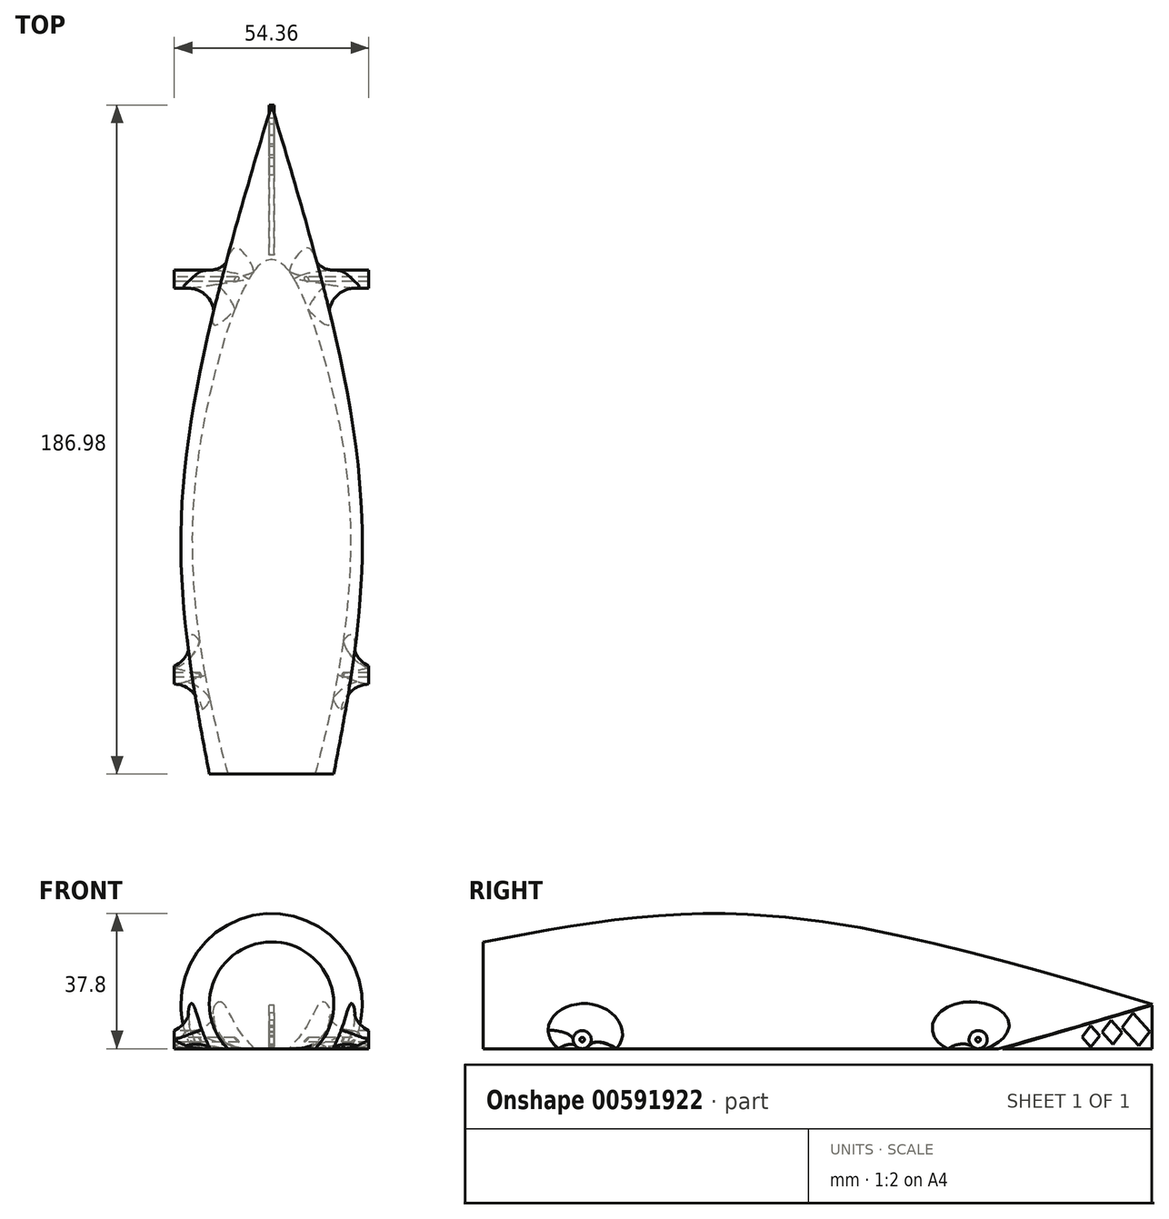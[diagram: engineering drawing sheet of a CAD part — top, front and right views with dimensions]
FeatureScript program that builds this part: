
annotation { "Feature Type Name" : "Feature", "Feature Type Description" : "" }
export const myFeature = defineFeature(function(context is Context, id is Id, definition is map)
    precondition{}
    {
        {
            var Q0;
            Q0=qCreatedBy(makeId("Top.planeOp"),FACE);
            cPlane(context, id + "F0", {"entities" : qUnion([Q0]), "cplaneType" : CPlaneType.OFFSET, "offset" : 7.37 * mm, "width" : 152.4 * mm, "height" : 152.4 * mm});
        }
        {
            var Q0;
            Q0=qCreatedBy(id+"F0.planeOp",FACE);
            var sketch = newSketch(context, id + "F1", { "sketchPlane" : qUnion([Q0])});
            skLineSegment(sketch, "E0", {"start": v(0, -99.9) * mm, "end": v(-17.4, -99.9) * mm});
            skFitSpline(sketch, "E1", {"points": [v(-17.4, -99.9) * mm, v(-24.98, -23.09) * mm, v(0, 87.08) * mm], "startDerivative": vector(-30.87, 162.6) * mm, "endDerivative": vector(62.7, 209.85) * mm});
            skLineSegment(sketch, "E2", {"start": v(0, -99.9) * mm, "end": v(0, 87.08) * mm});
            skSolve(sketch);
        }
        {
            var Q0;
            Q0=qSketchRegion(id+"F1",true);
            var Q1;
            Q1=sQuery(id+"F1.wireOp",EDGE,"E2");
            revolve(context, id + "F2", {"entities" : qUnion([Q0]), "axis" : qUnion([Q1]), "revolveType" : RevolveType.FULL});
        }
        {
            var Q0;
            Q0=qCreatedBy(makeId("Top.planeOp"),FACE);
            cPlane(context, id + "F3", {"entities" : qUnion([Q0]), "cplaneType" : CPlaneType.OFFSET, "offset" : 5.08 * mm, "oppositeDirection" : true, "width" : 152.4 * mm, "height" : 152.4 * mm});
        }
        {
            var Q0;
            Q0=qCreatedBy(id+"F3.planeOp",FACE);
            var sketch = newSketch(context, id + "F4", { "sketchPlane" : qUnion([Q0])});
            skLineSegment(sketch, "E3.bottom", {"start": v(73.32, 143.23) * mm, "end": v(-63.31, 143.23) * mm});
            skLineSegment(sketch, "E3.top", {"start": v(73.32, -152.23) * mm, "end": v(-63.31, -152.23) * mm});
            skLineSegment(sketch, "E3.left", {"start": v(73.32, 143.23) * mm, "end": v(73.32, -152.23) * mm});
            skLineSegment(sketch, "E3.right", {"start": v(-63.31, 143.23) * mm, "end": v(-63.31, -152.23) * mm});
            skSolve(sketch);
        }
        {
            var Q0;
            Q0=qSketchRegion(id+"F4",true);
            extrude(context, id + "F5", {"entities" : qUnion([Q0]), "operationType" : NewBodyOperationType.REMOVE, "oppositeDirection" : true, "depth" : 25.4 * mm, "offsetDistance" : 25.4 * mm});
        }
        {
            var Q0;
            Q0=qCreatedBy(makeId("Right.planeOp"),FACE);
            var sketch = newSketch(context, id + "F6", { "sketchPlane" : qUnion([Q0])});
            skLineSegment(sketch, "E4", {"start": v(45.18, -5.08) * mm, "end": v(87.03, 7.1) * mm});
            skLineSegment(sketch, "E5", {"start": v(87.03, 7.1) * mm, "end": v(87.03, -5.08) * mm});
            skLineSegment(sketch, "E6", {"start": v(87.03, -5.08) * mm, "end": v(45.18, -5.08) * mm});
            skLineSegment(sketch, "E7", {"start": v(86.3, -0.32) * mm, "end": v(81.67, 4.86) * mm});
            skLineSegment(sketch, "E8", {"start": v(81.67, 4.86) * mm, "end": v(78.67, 0.88) * mm});
            skLineSegment(sketch, "E9", {"start": v(78.67, 0.88) * mm, "end": v(83.3, -4.3) * mm});
            skLineSegment(sketch, "E10", {"start": v(83.3, -4.3) * mm, "end": v(86.3, -0.32) * mm});
            skLineSegment(sketch, "E11", {"start": v(75.51, 2.93) * mm, "end": v(73.01, -0.37) * mm});
            skLineSegment(sketch, "E12", {"start": v(73.01, -0.37) * mm, "end": v(76.08, -3.8) * mm});
            skLineSegment(sketch, "E13", {"start": v(76.08, -3.8) * mm, "end": v(78.58, -0.5) * mm});
            skLineSegment(sketch, "E14", {"start": v(78.58, -0.5) * mm, "end": v(75.51, 2.93) * mm});
            skLineSegment(sketch, "E15", {"start": v(67.45, -1.84) * mm, "end": v(69.85, 1.33) * mm});
            skLineSegment(sketch, "E16", {"start": v(69.85, 1.33) * mm, "end": v(72.33, -1.45) * mm});
            skLineSegment(sketch, "E17", {"start": v(72.33, -1.45) * mm, "end": v(69.92, -4.64) * mm});
            skLineSegment(sketch, "E18", {"start": v(69.92, -4.64) * mm, "end": v(67.45, -1.84) * mm});
            skSolve(sketch);
        }
        {
            var Q0;
            Q0=qSketchRegion(id+"F6",true);
            extrude(context, id + "F7", {"entities" : qUnion([Q0]), "endBound" : BoundingType.SYMMETRIC, "depth" : 1.42 * mm, "offsetDistance" : 25.4 * mm});
        }
        {
            var Q0;
            Q0=qCreatedBy(makeId("Right.planeOp"),FACE);
            var sketch = newSketch(context, id + "F8", { "sketchPlane" : qUnion([Q0])});
            skCircle(sketch, "E19", {"center": v(38.4, -2.54) * mm, "radius": 2.54 * mm});
            skCircle(sketch, "E20", {"center": v(38.4, -2.54) * mm, "radius": 0.64 * mm});
            skCircle(sketch, "E21", {"center": v(-72.27, -2.54) * mm, "radius": 2.54 * mm});
            skCircle(sketch, "E22", {"center": v(-72.27, -2.54) * mm, "radius": 0.64 * mm});
            skSolve(sketch);
        }
        {
            var Q0;
            Q0=qSketchRegion(id+"F8",true);
            extrude(context, id + "F9", {"entities" : qUnion([Q0]), "operationType" : NewBodyOperationType.ADD, "endBound" : BoundingType.SYMMETRIC, "depth" : 54.36 * mm, "offsetDistance" : 25.4 * mm});
        }
        {
            var Q0;
            Q0=makeQuery(id+"F9.boolean.opBoolean","INTERSECT",EDGE,{"disambiguationData":[OD(0.0)],"derivedFrom":[makeQuery(id+"F2.opRevolve","SWEPT_FACE",FACE,{"disambiguationData":[OSD([sQuery(id+"F1.wireOp",EDGE,"E1")])]}),makeQuery(id+"F9.opExtrude","SWEPT_FACE",FACE,{"disambiguationData":[OSD([sQuery(id+"F8.wireOp",EDGE,"E19")])]})]});
            var Q1;
            Q1=makeQuery(id+"F9.boolean.opBoolean","INTERSECT",EDGE,{"disambiguationData":[OD(1.0)],"derivedFrom":[makeQuery(id+"F2.opRevolve","SWEPT_FACE",FACE,{"disambiguationData":[OSD([sQuery(id+"F1.wireOp",EDGE,"E1")])]}),makeQuery(id+"F9.opExtrude","SWEPT_FACE",FACE,{"disambiguationData":[OSD([sQuery(id+"F8.wireOp",EDGE,"E19")])]})]});
            var Q2;
            Q2=makeQuery(id+"F9.boolean.opBoolean","INTERSECT",EDGE,{"disambiguationData":[OD(0.0)],"derivedFrom":[makeQuery(id+"F2.opRevolve","SWEPT_FACE",FACE,{"disambiguationData":[OSD([sQuery(id+"F1.wireOp",EDGE,"E1")])]}),makeQuery(id+"F9.opExtrude","SWEPT_FACE",FACE,{"disambiguationData":[OSD([sQuery(id+"F8.wireOp",EDGE,"E21")])]})]});
            var Q3;
            Q3=makeQuery(id+"F9.boolean.opBoolean","INTERSECT",EDGE,{"disambiguationData":[OD(1.0)],"derivedFrom":[makeQuery(id+"F2.opRevolve","SWEPT_FACE",FACE,{"disambiguationData":[OSD([sQuery(id+"F1.wireOp",EDGE,"E1")])]}),makeQuery(id+"F9.opExtrude","SWEPT_FACE",FACE,{"disambiguationData":[OSD([sQuery(id+"F8.wireOp",EDGE,"E21")])]})]});
            fillet(context, id + "F10", {"entities" : qUnion([Q0, Q1, Q2, Q3]), "radius" : 8.38 * mm, "tangentPropagation" : true, "allowEdgeOverflow" : false});
        }
        {
            var Q0;
            Q0=qCreatedBy(makeId("Right.planeOp"),FACE);
            var sketch = newSketch(context, id + "F11", { "sketchPlane" : qUnion([Q0])});
            skLineSegment(sketch, "E23", {"start": v(-99.72, 5.95) * mm, "end": v(-94.4, 6.5) * mm});
            skLineSegment(sketch, "E24", {"start": v(-94.4, 6.5) * mm, "end": v(-94.3, 5.92) * mm});
            skLineSegment(sketch, "E25", {"start": v(-94.3, 5.92) * mm, "end": v(-99.72, 5.95) * mm});
            skSolve(sketch);
        }
        {
            var Q0;
            Q0=qSketchRegion(id+"F11",true);
            extrude(context, id + "F12", {"entities" : qUnion([Q0]), "operationType" : NewBodyOperationType.ADD, "endBound" : BoundingType.SYMMETRIC, "depth" : 7.62 * mm, "offsetDistance" : 25.4 * mm});
        }
    });
